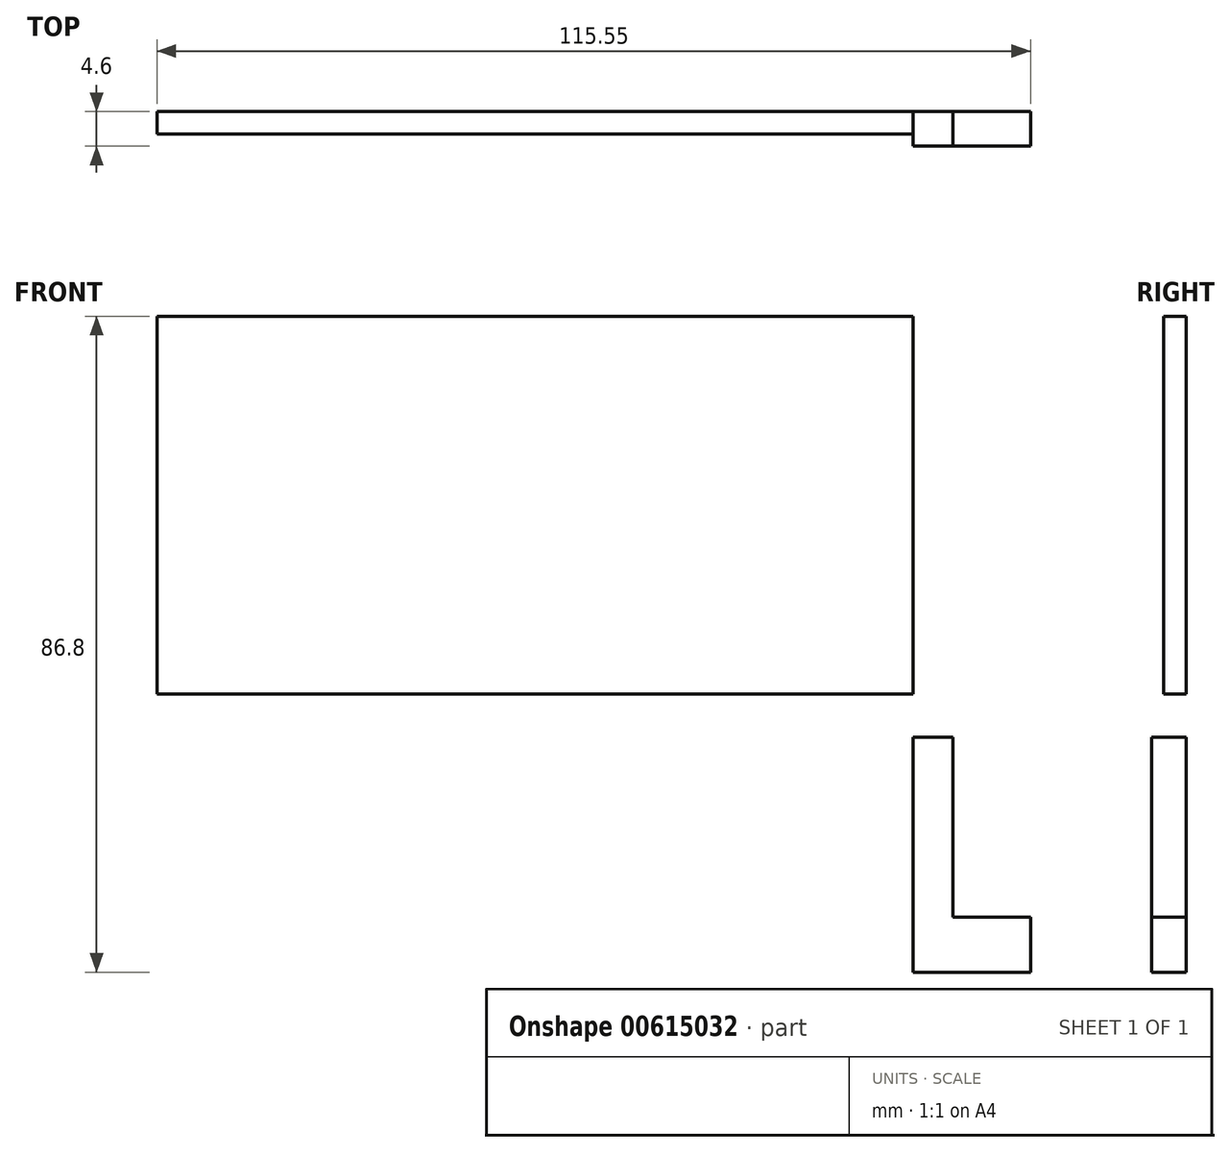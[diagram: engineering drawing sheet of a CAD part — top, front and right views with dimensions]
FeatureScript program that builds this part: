
annotation { "Feature Type Name" : "Feature", "Feature Type Description" : "" }
export const myFeature = defineFeature(function(context is Context, id is Id, definition is map)
    precondition{}
    {
        {
            var Q0;
            Q0=qCreatedBy(makeId("Front.planeOp"),FACE);
            var sketch = newSketch(context, id + "F0", { "sketchPlane" : qUnion([Q0])});
            skLineSegment(sketch, "E0.bottom", {"start": v(0, 0) * mm, "end": v(-100, 0) * mm});
            skLineSegment(sketch, "E0.top", {"start": v(0, 50) * mm, "end": v(-100, 50) * mm});
            skLineSegment(sketch, "E0.left", {"start": v(0, 0) * mm, "end": v(0, 50) * mm});
            skLineSegment(sketch, "E0.right", {"start": v(-100, 0) * mm, "end": v(-100, 50) * mm});
            skSolve(sketch);
        }
        {
            var Q0;
            Q0 = qSketchRegion(id + "F0", true);
            extrude(context, id + "F1", {"entities" : qUnion([Q0]), "depth" : 3 * mm, "offsetDistance" : 25 * mm});
        }
        {
            var Q0;
            Q0=qCreatedBy(makeId("Front.planeOp"),FACE);
            var sketch = newSketch(context, id + "F2", { "sketchPlane" : qUnion([Q0])});
            skLineSegment(sketch, "E1", {"start": v(0, -5.7) * mm, "end": v(0, -36.8) * mm});
            skLineSegment(sketch, "E2", {"start": v(0, -36.8) * mm, "end": v(15.55, -36.8) * mm});
            skLineSegment(sketch, "E3", {"start": v(15.55, -36.8) * mm, "end": v(15.55, -29.5) * mm});
            skLineSegment(sketch, "E4", {"start": v(15.55, -29.5) * mm, "end": v(5.26, -29.5) * mm});
            skLineSegment(sketch, "E5", {"start": v(5.26, -29.5) * mm, "end": v(5.26, -5.7) * mm});
            skLineSegment(sketch, "E6", {"start": v(5.26, -5.7) * mm, "end": v(0, -5.7) * mm});
            skLineSegment(sketch, "E7", {"start": v(21.35, -36.8) * mm, "end": v(21.35, -5.7) * mm});
            skSolve(sketch);
        }
        {
            var Q0;
            Q0 = qSketchRegion(id + "FS1yGeUYEz35CBH_1", true);
            var Q1;
            Q1 = qSketchRegion(id + "F2", true);
            extrude(context, id + "F3", {"entities" : qUnion([Q0, Q1]), "depth" : 4.6 * mm, "offsetDistance" : 25 * mm});
        }
    });
